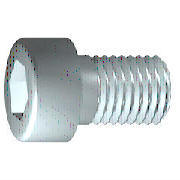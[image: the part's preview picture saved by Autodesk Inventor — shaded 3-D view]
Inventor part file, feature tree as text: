
AUTODESK INVENTOR PART (.ipt)
format: ipt  version: 2016 (Build 200138000, 138)  size: 196,608 bytes
history: native  units: mm (DEFAULTED — no unit token found)
features: sketch x2, extrude x1, plane x1, fillet x1
ambient origin geometry x7: Origin, YZ Plane, XY Plane, X Axis, Y Axis, Z Axis, Center Point
bodies: Solid1 (feature_tree), Body (feature_tree)
feature tree (5):
  extrude  "Slot"  Depth=3.0mm
  plane  "Work Plane1"
  fillet  "Fillet2"  Radius=3.0mm
  sketch  "Sketch1"  dims[d1=4.75mm d2=0.306825mm d3=3.0mm]
  sketch  "Sketch2"  dims[d4=1.3mm d5=60.0deg d6=3.0mm d7=3.0mm d8=2.886751mm d9=5.5mm d10=90.0deg d11=10.0mm d12=0.0mm d13=4.75mm d14=0.0mm d15=0.306725mm d16=0.306725mm d17=0.3mm d19=0.0mm d26=6.0mm d27=45.0deg d28=0.0mm d29=0.0mm d30=0.1mm]
